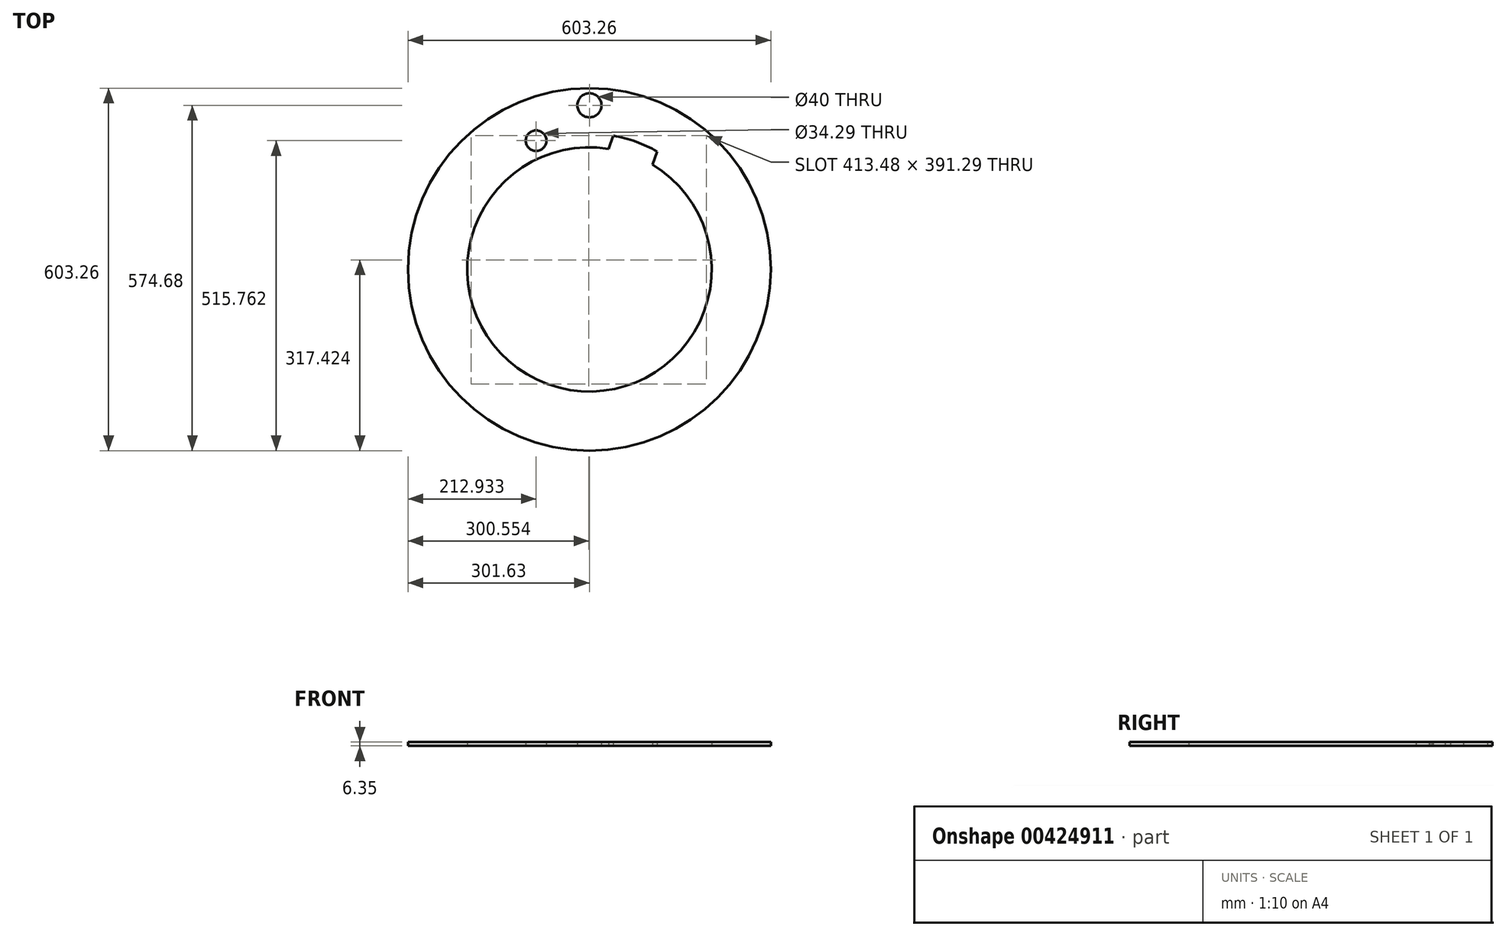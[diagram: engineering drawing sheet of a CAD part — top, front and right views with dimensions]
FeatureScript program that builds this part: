
annotation { "Feature Type Name" : "Feature", "Feature Type Description" : "" }
export const myFeature = defineFeature(function(context is Context, id is Id, definition is map)
    precondition{}
    {
        {
            var Q0;
            Q0=qCreatedBy(makeId("Top.planeOp"),FACE);
            var sketch = newSketch(context, id + "F0", { "sketchPlane" : qUnion([Q0])});
            skCircle(sketch, "E0", {"center": v(0, 0) * mm, "radius": 301.63 * mm});
            skCircle(sketch, "E1", {"center": v(0, 0) * mm, "radius": 203.2 * mm});
            skLineSegment(sketch, "E2", {"start": v(0, 0) * mm, "end": v(0, 301.63) * mm, "construction": true});
            skLineSegment(sketch, "E3", {"start": v(0, 0) * mm, "end": v(103.16, 283.43) * mm, "construction": true});
            skLineSegment(sketch, "E4", {"start": v(0, 0) * mm, "end": v(-115.43, 278.67) * mm, "construction": true});
            skCircle(sketch, "E5", {"center": v(0, 0) * mm, "radius": 231.78 * mm, "construction": true});
            skCircle(sketch, "E6", {"center": v(0, 0) * mm, "radius": 273.05 * mm, "construction": true});
            skCircle(sketch, "E7", {"center": v(-88.7, 214.13) * mm, "radius": 17.15 * mm});
            skCircle(sketch, "E8", {"center": v(0, 273.05) * mm, "radius": 20 * mm});
            skArc(sketch, "E9", {"start": v(112.57, 196.04) * mm, "mid": v(77.32, 212.43) * mm, "end": v(39.77, 222.53) * mm});
            skLineSegment(sketch, "E10.0", {"start": v(104.62, 174.2) * mm, "end": v(112.57, 196.04) * mm});
            skLineSegment(sketch, "E11.trimOffspring", {"start": v(31.83, 200.7) * mm, "end": v(39.77, 222.53) * mm});
            skSolve(sketch);
        }
        {
            var Q0;
            Q0 = qSketchRegion(id + "F0", true);
            var Q1;
            Q1=makeQuery(id+"F0.imprint","IMPRINT",FACE,{"disambiguationData":[TD([[makeQuery(id+"F0.imprint","IMPRINT",EDGE,{"derivedFrom":sQuery(id+"F0.wireOp",EDGE,"E9")}),1.0]])]});
            var Q2;
            Q2=makeQuery(id+"F0.imprint","IMPRINT",FACE,{"disambiguationData":[TD([[makeQuery(id+"F0.imprint","IMPRINT",EDGE,{"derivedFrom":sQuery(id+"F0.wireOp",EDGE,"E8")}),1.0]])]});
            var Q3;
            Q3=makeQuery(id+"F0.imprint","IMPRINT",FACE,{"disambiguationData":[TD([[makeQuery(id+"F0.imprint","IMPRINT",EDGE,{"derivedFrom":sQuery(id+"F0.wireOp",EDGE,"E7")}),1.0]])]});
            extrude(context, id + "F1", {"entities" : qUnion([Q0, Q1, Q2, Q3]), "depth" : 6.35 * mm});
        }
        {
            var Q0;
            Q0=makeQuery(id+"F0.imprint","IMPRINT",FACE,{"disambiguationData":[TD([[makeQuery(id+"F0.imprint","IMPRINT",EDGE,{"derivedFrom":sQuery(id+"F0.wireOp",EDGE,"E8")}),1.0]])]});
            extrude(context, id + "F2", {"entities" : qUnion([Q0]), "operationType" : NewBodyOperationType.REMOVE, "endBound" : BoundingType.THROUGH_ALL, "depth" : 25.4 * mm});
        }
        {
            var Q0;
            Q0=makeQuery(id+"F0.imprint","IMPRINT",FACE,{"disambiguationData":[TD([[makeQuery(id+"F0.imprint","IMPRINT",EDGE,{"derivedFrom":sQuery(id+"F0.wireOp",EDGE,"E9")}),1.0]])]});
            extrude(context, id + "F3", {"entities" : qUnion([Q0]), "operationType" : NewBodyOperationType.REMOVE, "endBound" : BoundingType.THROUGH_ALL, "depth" : 25.4 * mm});
        }
        {
            var Q0;
            Q0=makeQuery(id+"F0.imprint","IMPRINT",FACE,{"disambiguationData":[TD([[makeQuery(id+"F0.imprint","IMPRINT",EDGE,{"derivedFrom":sQuery(id+"F0.wireOp",EDGE,"E7")}),1.0]])]});
            extrude(context, id + "F4", {"entities" : qUnion([Q0]), "operationType" : NewBodyOperationType.REMOVE, "endBound" : BoundingType.THROUGH_ALL, "depth" : 25.4 * mm});
        }
    });
